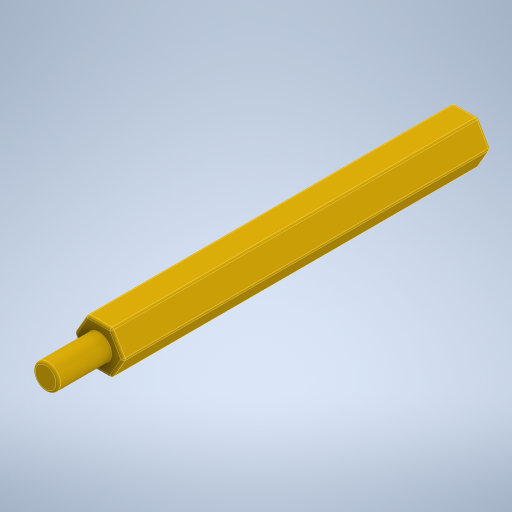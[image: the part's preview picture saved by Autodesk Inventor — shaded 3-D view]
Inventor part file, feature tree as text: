
AUTODESK INVENTOR PART (.ipt)
format: ipt  version: 2023 (Build 270158030, 158C)  size: 279,552 bytes
history: native  units: mm
features: extrude x3, fillet x3, sketch x3, other x1
ambient origin geometry x8: Origin, YZ Plane, XZ Plane, XY Plane, X Axis, Y Axis, Z Axis, Center Point
bodies: Body1 (feature_tree)
feature tree (10):
  other  "Sólido1"
  extrude  "Extrusión1"  Depth=40.0mm TaperAngle=0.0deg
  extrude  "Extrusión2"  Depth=5.8mm TaperAngle=0.0deg
  fillet  "Empalme1"  Radius=0.25mm
  fillet  "Empalme2"  Radius=0.25mm
  extrude  "Extrusión3"  Depth=4.0mm TaperAngle=0.0deg
  fillet  "Empalme3"  Radius=0.25mm
  sketch  "Boceto1"  dims[d0=4.65mm d1=40.0mm d2=0.0mm]
  sketch  "Boceto2"  dims[d3=2.75mm d4=5.8mm d5=0.0mm d6=0.25mm d7=0.25mm]
  sketch  "Boceto3"  dims[d8=2.4mm d9=4.0mm d10=0.0mm d11=0.25mm]
